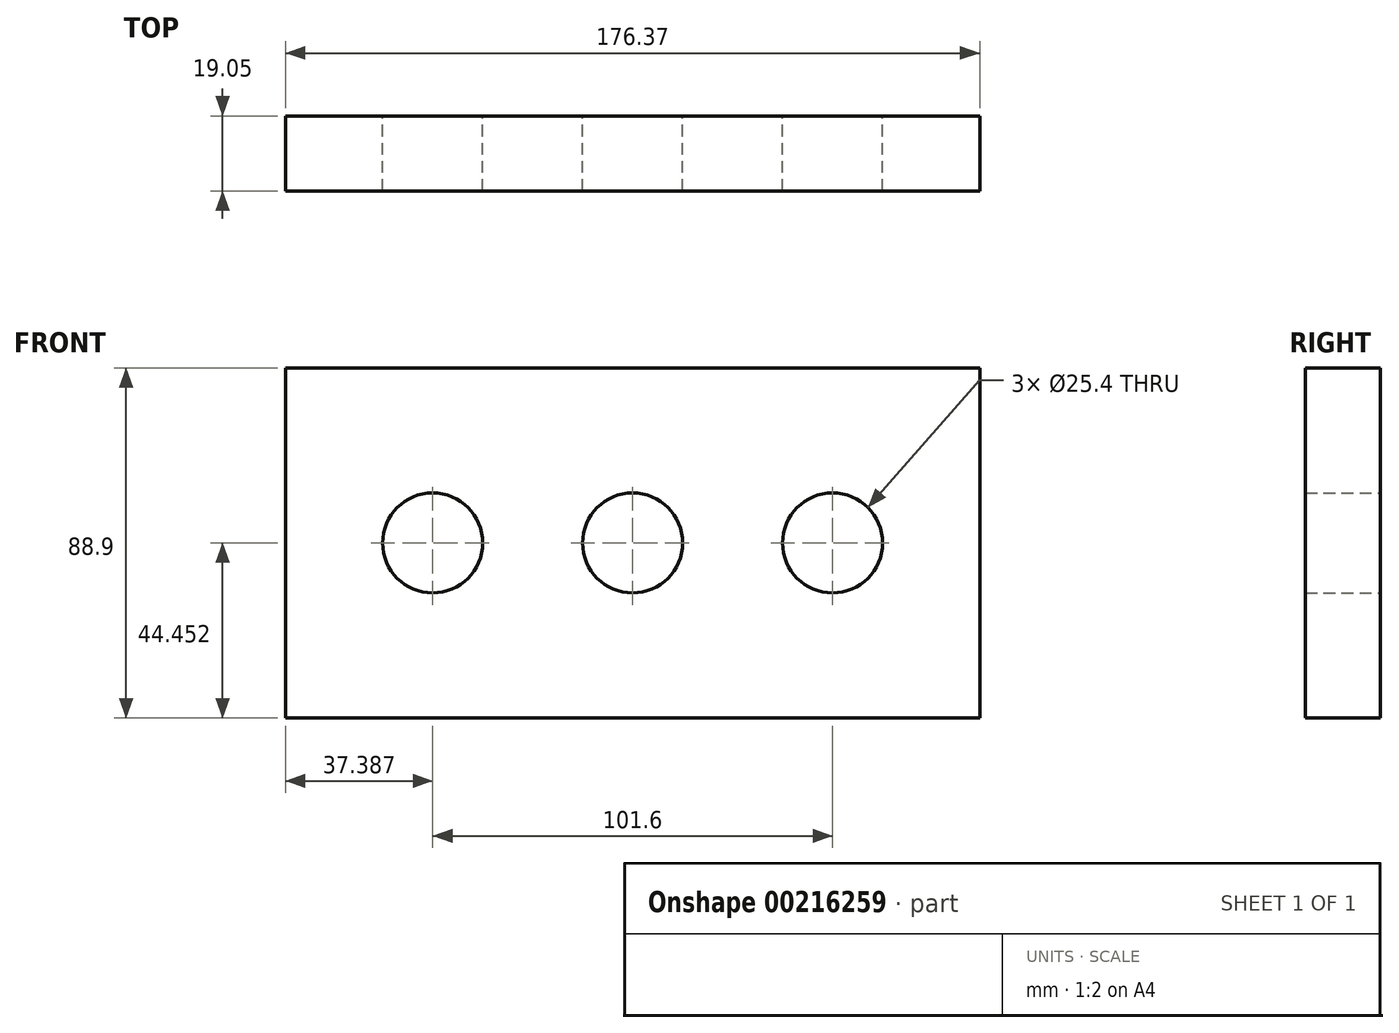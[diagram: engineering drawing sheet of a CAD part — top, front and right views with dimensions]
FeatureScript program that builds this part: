
annotation { "Feature Type Name" : "Feature", "Feature Type Description" : "" }
export const myFeature = defineFeature(function(context is Context, id is Id, definition is map)
    precondition{}
    {
        {
            var Q0;
            Q0=qCreatedBy(makeId("Front.planeOp"),FACE);
            var sketch = newSketch(context, id + "F0", { "sketchPlane" : qUnion([Q0])});
            skLineSegment(sketch, "E0", {"start": v(-3942.14, -2230.02) * mm, "end": v(-3765.77, -2230.02) * mm});
            skLineSegment(sketch, "E1", {"start": v(-3765.77, -2230.02) * mm, "end": v(-3765.77, -2318.92) * mm});
            skLineSegment(sketch, "E2", {"start": v(-3765.77, -2318.92) * mm, "end": v(-3942.14, -2318.92) * mm});
            skLineSegment(sketch, "E3", {"start": v(-3942.14, -2318.92) * mm, "end": v(-3942.14, -2230.02) * mm});
            skCircle(sketch, "E4", {"center": v(-3904.75, -2274.47) * mm, "radius": 12.7 * mm});
            skCircle(sketch, "E5", {"center": v(-3853.95, -2274.47) * mm, "radius": 12.7 * mm});
            skCircle(sketch, "E6", {"center": v(-3803.15, -2274.47) * mm, "radius": 12.7 * mm});
            skLineSegment(sketch, "E7", {"start": v(-3942.14, -2274.47) * mm, "end": v(-3765.77, -2274.47) * mm, "construction": true});
            skSolve(sketch);
        }
        {
            var Q0;
            Q0=makeQuery(id+"F0.imprint","IMPRINT",FACE,{"disambiguationData":[TD([[makeQuery(id+"F0.imprint","IMPRINT",EDGE,{"derivedFrom":sQuery(id+"F0.wireOp",EDGE,"E0")}),-1.0]])]});
            extrude(context, id + "F1", {"entities" : qUnion([Q0]), "depth" : 19.05 * mm});
        }
    });
